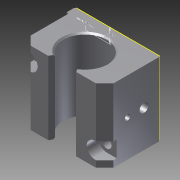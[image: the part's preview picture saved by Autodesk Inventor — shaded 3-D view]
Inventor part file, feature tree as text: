
AUTODESK INVENTOR PART (.ipt)
format: ipt  version: 2013 (Build 170138000, 138)  size: 143,360 bytes
history: native  units: in
note: dims shown in document units (in); Inventor stores cm internally (conversion verified against a paired STEP export)
features: sketch x1, imported_body x1
ambient origin geometry x8: Origin, YZ Plane, XZ Plane, XY Plane, X Axis, Y Axis, Z Axis, Center Point
feature tree (2):
  sketch  "Sketch1"  dims[d0=0.5315in d1=0.315in]
  imported_body  "Base1"
